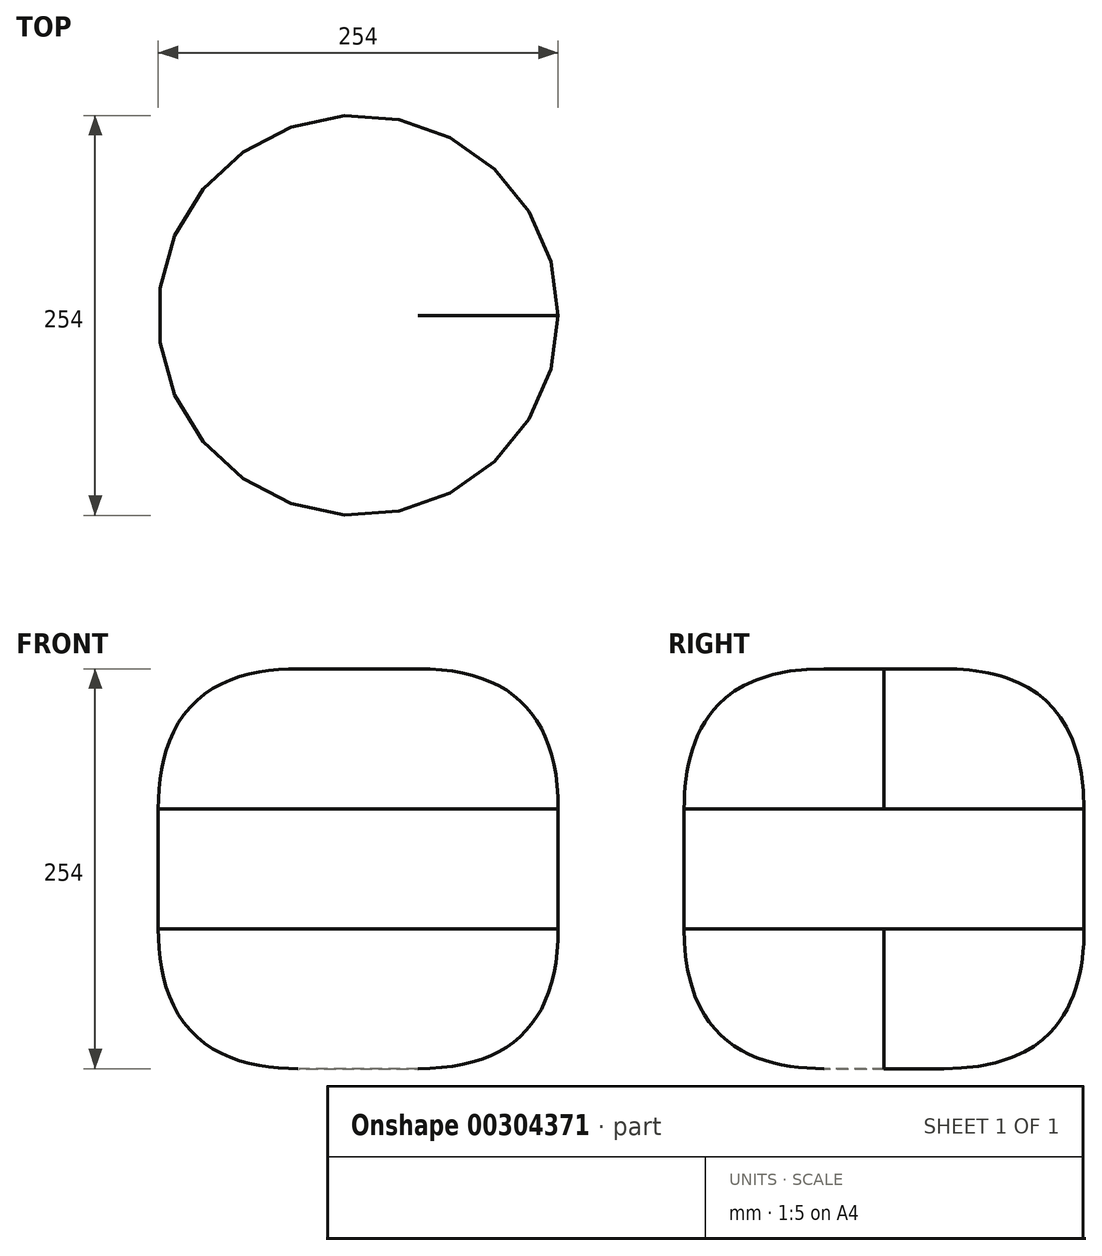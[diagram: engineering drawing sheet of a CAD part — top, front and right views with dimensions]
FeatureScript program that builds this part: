
annotation { "Feature Type Name" : "Feature", "Feature Type Description" : "" }
export const myFeature = defineFeature(function(context is Context, id is Id, definition is map)
    precondition{}
    {
        {
            var Q0;
            Q0=qCreatedBy(makeId("Top.planeOp"),FACE);
            var sketch = newSketch(context, id + "F0", { "sketchPlane" : qUnion([Q0])});
            skCircle(sketch, "E0", {"center": v(0, 0) * mm, "radius": 127 * mm});
            skLineSegment(sketch, "E1", {"start": v(0, 127) * mm, "end": v(0, -127) * mm, "construction": true});
            skSolve(sketch);
        }
        {
            var Q0;
            Q0=makeQuery(id+"F0.imprint","IMPRINT",FACE,{"disambiguationData":[TD([[makeQuery(id+"F0.imprint","IMPRINT",EDGE,{"derivedFrom":sQuery(id+"F0.wireOp",EDGE,"E0")}),1.0]])]});
            extrude(context, id + "F1", {"entities" : qUnion([Q0]), "endBound" : BoundingType.SYMMETRIC, "depth" : 254 * mm});
        }
        {
            var Q0;
            Q0=makeQuery(id+"F1.opExtrude","CAP_EDGE",EDGE,{"disambiguationData":[OSD([sQuery(id+"F0.wireOp",EDGE,"E0")])],"isStart":false});
            var Q1;
            Q1=makeQuery(id+"F1.opExtrude","CAP_EDGE",EDGE,{"disambiguationData":[OSD([sQuery(id+"F0.wireOp",EDGE,"E0")])],"isStart":true});
            fillet(context, id + "F2", {"entities" : qUnion([Q0, Q1]), "radius" : 88.9 * mm, "tangentPropagation" : true, "rho" : 0.5, "crossSection" : FilletCrossSection.CONIC, "allowEdgeOverflow" : false});
        }
    });
